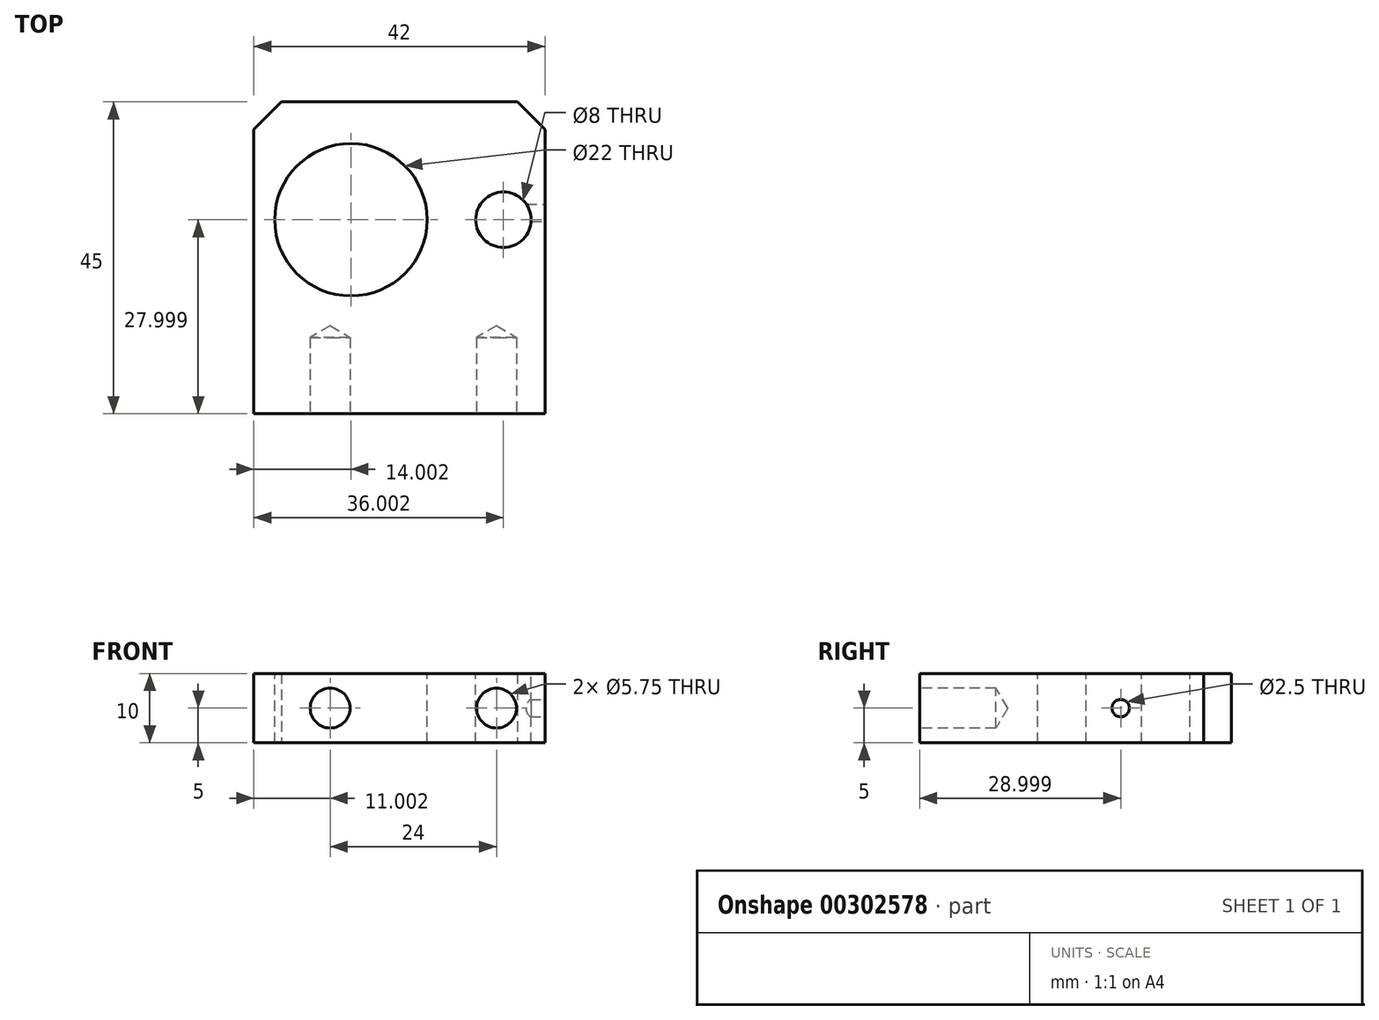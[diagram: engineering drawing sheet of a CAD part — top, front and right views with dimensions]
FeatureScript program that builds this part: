
annotation { "Feature Type Name" : "Feature", "Feature Type Description" : "" }
export const myFeature = defineFeature(function(context is Context, id is Id, definition is map)
    precondition{}
    {
        {
            var Q0;
            Q0=qCreatedBy(makeId("Top.planeOp"),FACE);
            var sketch = newSketch(context, id + "F0", { "sketchPlane" : qUnion([Q0])});
            skLineSegment(sketch, "E0.bottom", {"start": v(-6.53, -47.2) * mm, "end": v(35.47, -47.2) * mm});
            skLineSegment(sketch, "E0.top", {"start": v(-6.53, -2.2) * mm, "end": v(35.47, -2.2) * mm});
            skLineSegment(sketch, "E0.left", {"start": v(-6.53, -47.2) * mm, "end": v(-6.53, -2.2) * mm});
            skLineSegment(sketch, "E0.right", {"start": v(35.47, -47.2) * mm, "end": v(35.47, -2.2) * mm});
            skLineSegment(sketch, "E1", {"start": v(-6.53, -2.2) * mm, "end": v(-6.53, -6.2) * mm});
            skLineSegment(sketch, "E2", {"start": v(-6.53, -2.2) * mm, "end": v(-2.53, -2.2) * mm});
            skLineSegment(sketch, "E3", {"start": v(-6.53, -6.2) * mm, "end": v(-2.53, -2.2) * mm});
            skLineSegment(sketch, "E4", {"start": v(35.47, -2.2) * mm, "end": v(31.47, -2.2) * mm});
            skLineSegment(sketch, "E5", {"start": v(35.47, -2.2) * mm, "end": v(35.47, -6.2) * mm});
            skLineSegment(sketch, "E6", {"start": v(31.47, -2.2) * mm, "end": v(35.47, -6.2) * mm});
            skSolve(sketch);
        }
        {
            var Q0;
            Q0=makeQuery(id+"F0.imprint","IMPRINT",FACE,{"disambiguationData":[TD([[makeQuery(id+"F0.imprint","IMPRINT",EDGE,{"derivedFrom":sQuery(id+"F0.wireOp",EDGE,"E0.bottom")}),1.0]])]});
            extrude(context, id + "F1", {"entities" : qUnion([Q0]), "depth" : 10 * mm});
        }
        {
            var Q0;
            Q0=makeQuery(id+"F1.opExtrude","CAP_FACE",FACE,{"disambiguationData":[OSD([sQuery(id+"F0.wireOp",EDGE,"E0.bottom"),sQuery(id+"F0.wireOp",EDGE,"E0.top"),sQuery(id+"F0.wireOp",EDGE,"E0.left"),sQuery(id+"F0.wireOp",EDGE,"E0.right"),sQuery(id+"F0.wireOp",EDGE,"E3"),sQuery(id+"F0.wireOp",EDGE,"E6")])],"isStart":false});
            var sketch = newSketch(context, id + "F2", { "sketchPlane" : qUnion([Q0])});
            skLineSegment(sketch, "E7", {"start": v(35.47, -19.2) * mm, "end": v(29.47, -19.2) * mm});
            skLineSegment(sketch, "E8", {"start": v(35.47, -47.2) * mm, "end": v(35.47, -19.2) * mm});
            skLineSegment(sketch, "E9", {"start": v(29.47, -19.2) * mm, "end": v(7.47, -19.2) * mm});
            skSolve(sketch);
        }
        {
            var Q0;
            Q0=sQuery(id+"F2.wireOp",VERTEX,"CIvIWWRe-vlt0-gAGz-4n0y-XakRUTotrNb2.end");
            var Q1;
            Q1=sQuery(id+"F2.wireOp",VERTEX,"E9.end");
            var Q2;
            Q2=makeQuery(id+"F1.opExtrude","SWEPT_BODY",BODY,{"disambiguationData":[OSD([sQuery(id+"F0.wireOp",EDGE,"E0.bottom"),sQuery(id+"F0.wireOp",EDGE,"E0.top"),sQuery(id+"F0.wireOp",EDGE,"E0.left"),sQuery(id+"F0.wireOp",EDGE,"E0.right"),sQuery(id+"F0.wireOp",EDGE,"E3"),sQuery(id+"F0.wireOp",EDGE,"E6")])]});
            hole(context, id + "F3", {"style" : HoleStyle.SIMPLE, "endStyle" : HoleEndStyle.THROUGH, "holeDiameter" : 22 * mm, "tappedDepth" : 12 * mm, "tapClearance" : 3, "locations" : qUnion([Q0, Q1]), "scope" : qUnion([Q2])});
        }
        {
            var Q0;
            Q0=sQuery(id+"F2.wireOp",VERTEX,"E7.end");
            var Q1;
            Q1=makeQuery(id+"F1.opExtrude","SWEPT_BODY",BODY,{"disambiguationData":[OSD([sQuery(id+"F0.wireOp",EDGE,"E0.bottom"),sQuery(id+"F0.wireOp",EDGE,"E0.top"),sQuery(id+"F0.wireOp",EDGE,"E0.left"),sQuery(id+"F0.wireOp",EDGE,"E0.right"),sQuery(id+"F0.wireOp",EDGE,"E3"),sQuery(id+"F0.wireOp",EDGE,"E6")])]});
            hole(context, id + "F4", {"style" : HoleStyle.SIMPLE, "endStyle" : HoleEndStyle.THROUGH, "holeDiameter" : 8 * mm, "tappedDepth" : 12 * mm, "tapClearance" : 3, "locations" : qUnion([Q0]), "scope" : qUnion([Q1])});
        }
        {
            var Q0;
            Q0=makeQuery(id+"F1.opExtrude","SWEPT_FACE",FACE,{"disambiguationData":[OSD([sQuery(id+"F0.wireOp",EDGE,"E0.right")])]});
            var sketch = newSketch(context, id + "F5", { "sketchPlane" : qUnion([Q0])});
            skLineSegment(sketch, "E10", {"start": v(-47.2, 10) * mm, "end": v(-18.2, 10) * mm});
            skLineSegment(sketch, "E11", {"start": v(-18.2, 10) * mm, "end": v(-18.2, 0) * mm});
            skPoint(sketch, "E12", {"position": v(-18.2, 5) * mm});
            skSolve(sketch);
        }
        {
            var Q0;
            Q0=sQuery(id+"F5.wireOp",VERTEX,"E12");
            var Q1;
            Q1=makeQuery(id+"F1.opExtrude","SWEPT_BODY",BODY,{"disambiguationData":[OSD([sQuery(id+"F0.wireOp",EDGE,"E0.bottom"),sQuery(id+"F0.wireOp",EDGE,"E0.top"),sQuery(id+"F0.wireOp",EDGE,"E0.left"),sQuery(id+"F0.wireOp",EDGE,"E0.right"),sQuery(id+"F0.wireOp",EDGE,"E3"),sQuery(id+"F0.wireOp",EDGE,"E6")])]});
            hole(context, id + "F6", {"style" : HoleStyle.SIMPLE, "endStyle" : HoleEndStyle.BLIND, "holeDiameter" : 2.5 * mm, "holeDepth" : 5 * mm, "tappedDepth" : 12 * mm, "tapClearance" : 3, "locations" : qUnion([Q0]), "scope" : qUnion([Q1])});
        }
        {
            var Q0;
            Q0=makeQuery(id+"F1.opExtrude","SWEPT_FACE",FACE,{"disambiguationData":[OSD([sQuery(id+"F0.wireOp",EDGE,"E0.bottom")])]});
            var sketch = newSketch(context, id + "F7", { "sketchPlane" : qUnion([Q0])});
            skLineSegment(sketch, "E13", {"start": v(-6.53, 5) * mm, "end": v(35.47, 5) * mm});
            skLineSegment(sketch, "E14", {"start": v(35.47, 5) * mm, "end": v(33.47, 5) * mm});
            skLineSegment(sketch, "E15", {"start": v(33.47, 5) * mm, "end": v(28.47, 5) * mm});
            skLineSegment(sketch, "E16", {"start": v(28.47, 5) * mm, "end": v(4.47, 5) * mm});
            skSolve(sketch);
        }
        {
            var Q0;
            Q0=sQuery(id+"F7.wireOp",VERTEX,"E15.end");
            var Q1;
            Q1=sQuery(id+"F7.wireOp",VERTEX,"E16.end");
            var Q2;
            Q2=makeQuery(id+"F1.opExtrude","SWEPT_BODY",BODY,{"disambiguationData":[OSD([sQuery(id+"F0.wireOp",EDGE,"E0.bottom"),sQuery(id+"F0.wireOp",EDGE,"E0.top"),sQuery(id+"F0.wireOp",EDGE,"E0.left"),sQuery(id+"F0.wireOp",EDGE,"E0.right"),sQuery(id+"F0.wireOp",EDGE,"E3"),sQuery(id+"F0.wireOp",EDGE,"E6")])]});
            hole(context, id + "F8", {"style" : HoleStyle.SIMPLE, "endStyle" : HoleEndStyle.BLIND, "holeDiameter" : 5.75 * mm, "holeDepth" : 11 * mm, "tappedDepth" : 12 * mm, "tapClearance" : 3, "locations" : qUnion([Q0, Q1]), "scope" : qUnion([Q2])});
        }
    });
